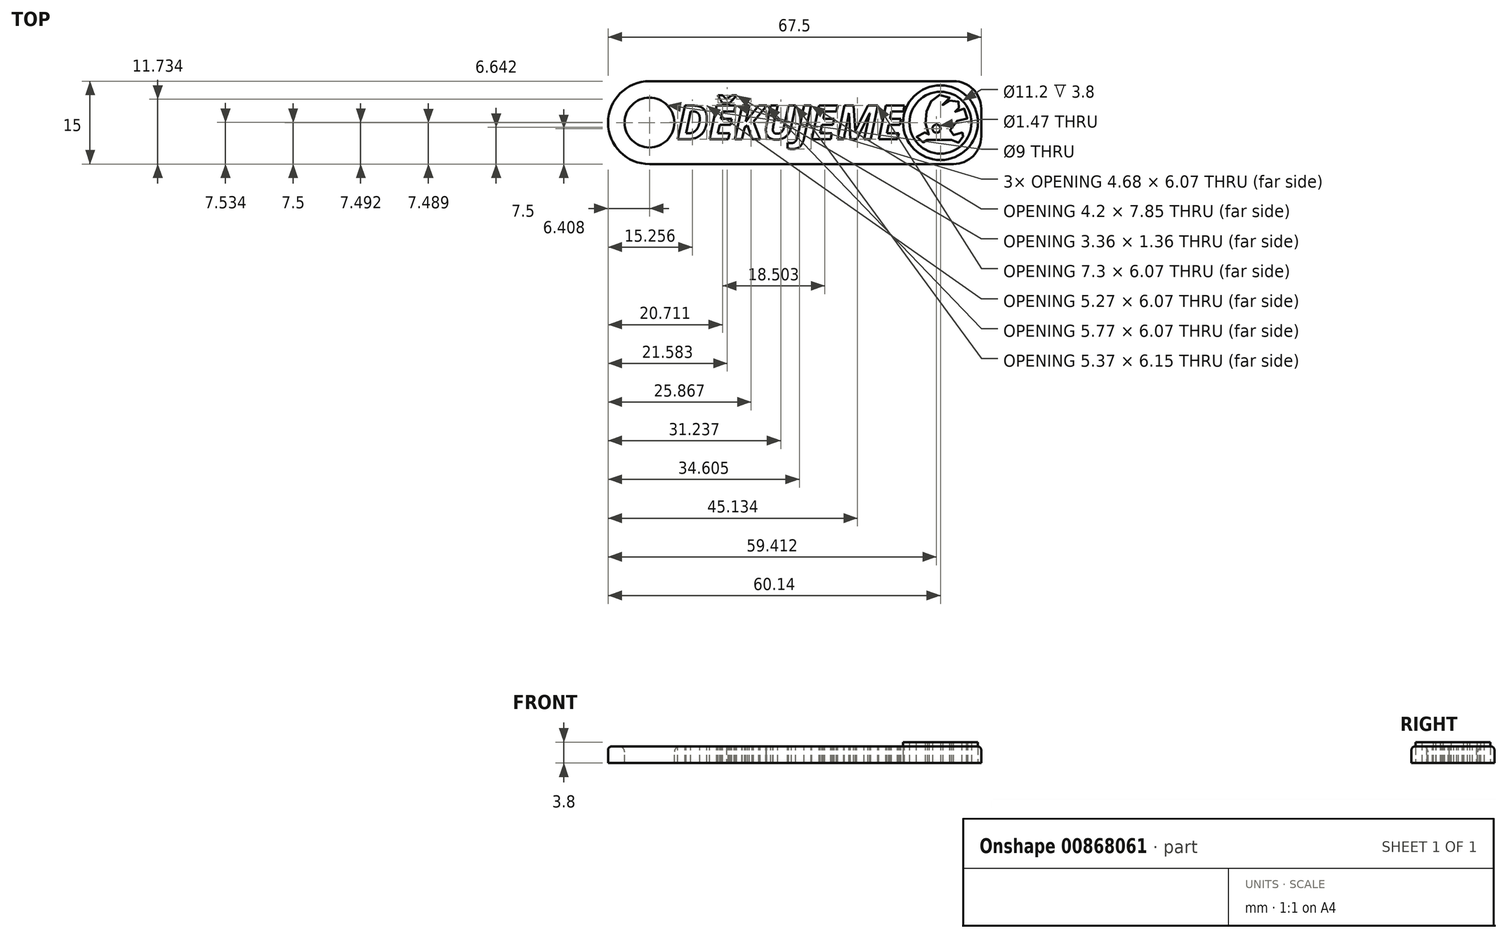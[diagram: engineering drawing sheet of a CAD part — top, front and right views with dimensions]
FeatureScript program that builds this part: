
annotation { "Feature Type Name" : "Feature", "Feature Type Description" : "" }
export const myFeature = defineFeature(function(context is Context, id is Id, definition is map)
    precondition{}
    {
        {
            var Q0;
            Q0=qCreatedBy(makeId("Top.planeOp"),FACE);
            var sketch = newSketch(context, id + "F0", { "sketchPlane" : qUnion([Q0])});
            skLineSegment(sketch, "E0.bottom", {"start": v(30, -7.5) * mm, "end": v(-30, -7.5) * mm});
            skLineSegment(sketch, "E0.top", {"start": v(30, 7.5) * mm, "end": v(-30, 7.5) * mm});
            skLineSegment(sketch, "E0.left", {"start": v(30, -7.5) * mm, "end": v(30, 7.5) * mm});
            skLineSegment(sketch, "E0.right", {"start": v(-30, -7.5) * mm, "end": v(-30, 7.5) * mm});
            skPoint(sketch, "E0.middle", {"position": v(0, 0) * mm});
            skCircle(sketch, "E1", {"center": v(-30, 0) * mm, "radius": 7.5 * mm});
            skCircle(sketch, "E2", {"center": v(-30, 0) * mm, "radius": 4.5 * mm});
            skSolve(sketch);
        }
        {
            var Q0;
            {var subQ0=sQuery(id+"F0.wireOp",EDGE,"rIMfdM6R-3KVO-rwKb-w4Yd-tlX4Zi2bp9xC.top");var subQ1=sQuery(id+"F0.wireOp",EDGE,"E0.left");var subQ2=makeQuery(id+"F0.imprint","INTERSECT",VERTEX,{"derivedFrom":[subQ1,subQ0]});Q0=makeQuery(id+"F0.imprint","IMPRINT",FACE,{"disambiguationData":[TD([[makeQuery(id+"F0.imprint","IMPRINT",EDGE,{"disambiguationData":[TD([[subQ2,-1.0]])],"derivedFrom":subQ1}),1.0]])]});}
            var Q1;
            {var subQ1=sQuery(id+"F0.wireOp",EDGE,"E0.right");var subQ3=sQuery(id+"F0.wireOp",EDGE,"E2");var subQ4=makeQuery(id+"F0.imprint","INTERSECT",VERTEX,{"disambiguationData":[OD(0.0)],"derivedFrom":[subQ1,subQ3]});Q1=makeQuery(id+"F0.imprint","IMPRINT",FACE,{"disambiguationData":[TD([[makeQuery(id+"F0.imprint","IMPRINT",EDGE,{"disambiguationData":[TD([[subQ4,-1.0]])],"derivedFrom":subQ3}),-1.0]])]});}
            var Q2;
            {var subQ1=sQuery(id+"F0.wireOp",EDGE,"E0.right");var subQ3=sQuery(id+"F0.wireOp",EDGE,"E2");var subQ4=makeQuery(id+"F0.imprint","INTERSECT",VERTEX,{"disambiguationData":[OD(0.0)],"derivedFrom":[subQ1,subQ3]});Q2=makeQuery(id+"F0.imprint","IMPRINT",FACE,{"disambiguationData":[TD([[makeQuery(id+"F0.imprint","IMPRINT",EDGE,{"disambiguationData":[TD([[subQ4,1.0]])],"derivedFrom":subQ3}),-1.0]])]});}
            extrude(context, id + "F1", {"entities" : qUnion([Q0, Q1, Q2]), "oppositeDirection" : true, "depth" : 3 * mm, "offsetDistance" : 25 * mm});
        }
        {
            var Q0;
            Q0=makeQuery(id+"F1.opExtrude","CAP_FACE",FACE,{"disambiguationData":[OSD([sQuery(id+"F0.wireOp",EDGE,"E0.bottom"),sQuery(id+"F0.wireOp",EDGE,"E0.top"),sQuery(id+"F0.wireOp",EDGE,"E0.left"),sQuery(id+"F0.wireOp",EDGE,"E0.right")])],"isStart":false});
            var sketch = newSketch(context, id + "F2", { "sketchPlane" : qUnion([Q0])});
            skCircle(sketch, "E3", {"center": v(22.64, 0.01) * mm, "radius": 6.76 * mm});
            skPoint(sketch, "E3.first.point", {"position": v(15.89, 0.22) * mm});
            skPoint(sketch, "E3.second.point", {"position": v(29.4, 0.22) * mm});
            skPoint(sketch, "E3.third.point", {"position": v(22.56, 6.77) * mm});
            skCircle(sketch, "E4", {"center": v(22.64, 0.01) * mm, "radius": 5.6 * mm});
            skCircle(sketch, "E5", {"center": v(21.91, 1.1) * mm, "radius": 0.74 * mm});
            skPoint(sketch, "E5.first.point", {"position": v(21.18, 1.12) * mm});
            skPoint(sketch, "E5.second.point", {"position": v(22.65, 1.1) * mm});
            skPoint(sketch, "E5.third.point", {"position": v(21.98, 1.83) * mm});
            skLineSegment(sketch, "E6", {"start": v(20.25, 3.15) * mm, "end": v(24.65, 3.15) * mm});
            skFitSpline(sketch, "E7", {"points": [v(24.65, 3.15) * mm, v(24.74, 3.15) * mm, v(24.95, 3.22) * mm, v(25.1, 3.3) * mm, v(25.34, 3.48) * mm, v(25.56, 3.58) * mm, v(25.73, 3.6) * mm, v(26.25, 3.6) * mm, v(26.3, 3.58) * mm, v(26.32, 3.49) * mm, v(26.35, 3.3) * mm, v(26.5, 2.92) * mm, v(26.7, 2.56) * mm, v(26.91, 2.33) * mm, v(27.21, 2.08) * mm, v(27.3, 2) * mm, v(27.3, 1.9) * mm, v(27.24, 1.83) * mm, v(27.1, 1.81) * mm, v(25.96, 1.81) * mm, v(25.85, 1.83) * mm, v(25.53, 2) * mm, v(25.32, 2.12) * mm, v(25.18, 2.2) * mm, v(25.06, 2.26) * mm, v(24.95, 2.28) * mm, v(24.28, 2.28) * mm, v(24.23, 2.27) * mm, v(24.22, 2.21) * mm, v(24.25, 1.87) * mm, v(24.36, 1.35) * mm, v(24.6, 0.8) * mm, v(24.9, 0.38) * mm, v(25.25, 0.01) * mm, v(25.68, -0.28) * mm, v(26.23, -0.5) * mm, v(26.76, -0.63) * mm, v(27.27, -0.66) * mm, v(27.42, -0.7) * mm, v(27.5, -0.77) * mm, v(27.56, -0.89) * mm, v(27.53, -1.08) * mm, v(27.3, -1.84) * mm, v(27.01, -2.41) * mm, v(26.88, -2.52) * mm, v(26.7, -2.56) * mm, v(26.53, -2.55) * mm, v(25.97, -2.35) * mm, v(25.5, -2.09) * mm, v(25.2, -1.92) * mm, v(25.1, -1.9) * mm, v(25.01, -1.94) * mm, v(24.97, -2.03) * mm, v(24.97, -2.12) * mm, v(25.33, -2.38) * mm, v(26.07, -2.73) * mm, v(26.37, -2.84) * mm, v(26.47, -2.93) * mm, v(26.5, -3.11) * mm, v(26.4, -3.32) * mm, v(25.95, -3.75) * mm, v(25.32, -4.22) * mm, v(25.1, -4.33) * mm, v(24.89, -4.35) * mm, v(24.77, -4.33) * mm, v(24.25, -3.95) * mm, v(23.48, -3.25) * mm, v(23.32, -3.06) * mm, v(23.26, -3) * mm, v(23.15, -3) * mm, v(23.05, -3.1) * mm, v(23.04, -3.2) * mm, v(23.1, -3.3) * mm, v(23.48, -3.7) * mm, v(24.03, -4.2) * mm, v(24.27, -4.39) * mm, v(24.3, -4.5) * mm, v(24.28, -4.61) * mm, v(24.18, -4.74) * mm, v(23.52, -4.92) * mm, v(22.82, -5) * mm, v(22.33, -5) * mm, v(22.05, -4.91) * mm, v(21.74, -4.73) * mm, v(21.33, -4.33) * mm, v(20.93, -3.83) * mm, v(20.6, -3.28) * mm, v(20.41, -2.87) * mm, v(20.26, -2.53) * mm, v(20.12, -2.11) * mm, v(19.99, -1.57) * mm, v(19.91, -1) * mm, v(19.9, -0.33) * mm, v(19.92, 0.16) * mm, v(20.03, 0.88) * mm, v(20.23, 1.51) * mm, v(20.35, 1.8) * mm, v(20.5, 2.12) * mm, v(20.58, 2.26) * mm, v(20.58, 2.3) * mm, v(20.19, 2.28) * mm, v(20.16, 2.27) * mm, v(20.14, 2.25) * mm, v(20.04, 2.12) * mm, v(19.88, 1.89) * mm, v(19.8, 1.82) * mm, v(19.58, 1.82) * mm, v(19.44, 1.85) * mm, v(19.13, 1.96) * mm, v(18.8, 2.15) * mm, v(18.5, 2.4) * mm, v(18.22, 2.7) * mm, v(18.23, 2.72) * mm, v(18.47, 2.99) * mm, v(18.78, 3.24) * mm, v(19.16, 3.47) * mm, v(19.51, 3.58) * mm, v(19.65, 3.6) * mm, v(19.87, 3.6) * mm, v(19.98, 3.54) * mm, v(20.07, 3.37) * mm, v(20.1, 3.25) * mm, v(20.13, 3.19) * mm, v(20.17, 3.15) * mm, v(20.25, 3.15) * mm], "startDerivative": vector(18.44, -2.13) * mm, "endDerivative": vector(19.87, 2.22) * mm});
            skSolve(sketch);
        }
        {
            var Q0;
            Q0=makeQuery(id+"F2.imprint","IMPRINT",FACE,{"disambiguationData":[TD([[makeQuery(id+"F2.imprint","IMPRINT",EDGE,{"derivedFrom":sQuery(id+"F2.wireOp",EDGE,"E5")}),-1.0]])]});
            var Q1;
            Q1=makeQuery(id+"F2.imprint","IMPRINT",FACE,{"disambiguationData":[TD([[makeQuery(id+"F2.imprint","IMPRINT",EDGE,{"derivedFrom":sQuery(id+"F2.wireOp",EDGE,"E3")}),1.0]])]});
            var Q2;
            Q2=makeQuery(id+"F1.opExtrude","CAP_FACE",FACE,{"disambiguationData":[OSD([sQuery(id+"F0.wireOp",EDGE,"E0.bottom"),sQuery(id+"F0.wireOp",EDGE,"E0.top"),sQuery(id+"F0.wireOp",EDGE,"E0.left"),sQuery(id+"F0.wireOp",EDGE,"E1"),sQuery(id+"F0.wireOp",EDGE,"E2")])],"isStart":true});
            var Q3;
            Q3=makeQuery(id+"F1.opExtrude","SWEPT_BODY",BODY,{"disambiguationData":[OSD([sQuery(id+"F0.wireOp",EDGE,"E0.bottom"),sQuery(id+"F0.wireOp",EDGE,"E0.top"),sQuery(id+"F0.wireOp",EDGE,"E0.left"),sQuery(id+"F0.wireOp",EDGE,"E1"),sQuery(id+"F0.wireOp",EDGE,"E2")])]});
            extrude(context, id + "F3", {"entities" : qUnion([Q0, Q1]), "oppositeDirection" : true, "depth" : 3.8 * mm, "endBoundEntityFace" : qUnion([Q2]), "endBoundEntityBody" : qUnion([Q3]), "offsetDistance" : 25 * mm});
        }
        {
            var Q0;
            Q0=makeQuery(id+"F1.opExtrude","CAP_FACE",FACE,{"disambiguationData":[OSD([sQuery(id+"F0.wireOp",EDGE,"E0.bottom"),sQuery(id+"F0.wireOp",EDGE,"E0.top"),sQuery(id+"F0.wireOp",EDGE,"E0.left"),sQuery(id+"F0.wireOp",EDGE,"E1"),sQuery(id+"F0.wireOp",EDGE,"E2")])],"isStart":true});
            var sketch = newSketch(context, id + "F4", { "sketchPlane" : qUnion([Q0])});
            skText(sketch, "E8", { "text": "DĚKUJEME", "fontName": "OpenSans-BoldItalic.ttf"});
            const initialGuessF4  = {"E8": [-0.0251, -0.003, 1, 0, 0.00612]};
            skSetInitialGuess(sketch, initialGuessF4);
            skSolve(sketch);
        }
        {
            var Q0;
            Q0 = qSketchRegion(id + "F4", true);
            extrude(context, id + "F5", {"entities" : qUnion([Q0]), "operationType" : NewBodyOperationType.REMOVE, "oppositeDirection" : true, "depth" : 25 * mm, "offsetDistance" : 25 * mm});
        }
        {
            var Q0;
            Q0=makeQuery(id+"F1.opExtrude","SWEPT_EDGE",EDGE,{"disambiguationData":[OSD([sQuery(id+"F0.wireOp",EDGE,"E0.top"),sQuery(id+"F0.wireOp",EDGE,"E0.left")])]});
            var Q1;
            Q1=makeQuery(id+"F1.opExtrude","SWEPT_EDGE",EDGE,{"disambiguationData":[OSD([sQuery(id+"F0.wireOp",EDGE,"E0.bottom"),sQuery(id+"F0.wireOp",EDGE,"E0.left")])]});
            fillet(context, id + "F6", {"entities" : qUnion([Q0, Q1]), "tangentPropagation" : true, "radius" : 5 * mm, "defaultsChanged" : false, "vertexSettings" : [], "allowEdgeOverflow" : false});
        }
        {
            var Q0;
            Q0=makeQuery(id+"F1.opExtrude","CAP_EDGE",EDGE,{"disambiguationData":[OSD([sQuery(id+"F0.wireOp",EDGE,"E0.top")])],"isStart":true});
            fillet(context, id + "F7", {"entities" : qUnion([Q0]), "tangentPropagation" : true, "radius" : 0.6 * mm, "defaultsChanged" : true, "vertexSettings" : [], "allowEdgeOverflow" : false});
        }
        {
            var Q0;
            Q0=makeQuery(id+"F1.opExtrude","CAP_EDGE",EDGE,{"disambiguationData":[OSD([sQuery(id+"F0.wireOp",EDGE,"E2")])],"isStart":true});
            fillet(context, id + "F8", {"entities" : qUnion([Q0]), "tangentPropagation" : true, "radius" : 1 * mm, "defaultsChanged" : true, "vertexSettings" : [], "allowEdgeOverflow" : false});
        }
    });
